AUTODESK INVENTOR PART (.ipt)
format: ipt  version: 2021 (Build 250183000, 183)  size: 152,576 bytes
history: native  units: mm
features: extrude x2, fillet x1, other x1, sketch x1
ambient origin geometry x8: Origin, YZ Plane, XZ Plane, XY Plane, X Axis, Y Axis, Z Axis, Center Point
bodies: Solid1 (feature_tree)
feature tree (5):
  extrude  "arm"  Depth=40.0mm
  extrude  "rod_hole"  Depth=20.0mm
  fillet  "rot_round"  Radius=10.0mm
  other  "arm_sketch"
  sketch  "Sketch5"  dims[d0=20.0mm d1=40.0mm d2=20.0mm d3=10.0mm d4=14.0mm d5=10.0mm d6=0.0mm d63=12.0mm d64=12.0mm d66=10.0mm d67=14.0mm d68=4.0mm d69=4.0mm d70=5.0mm d71=5.0mm d72=5.0mm d73=5.0mm d74=0.0mm d75=0.0mm d76=4.0mm]
